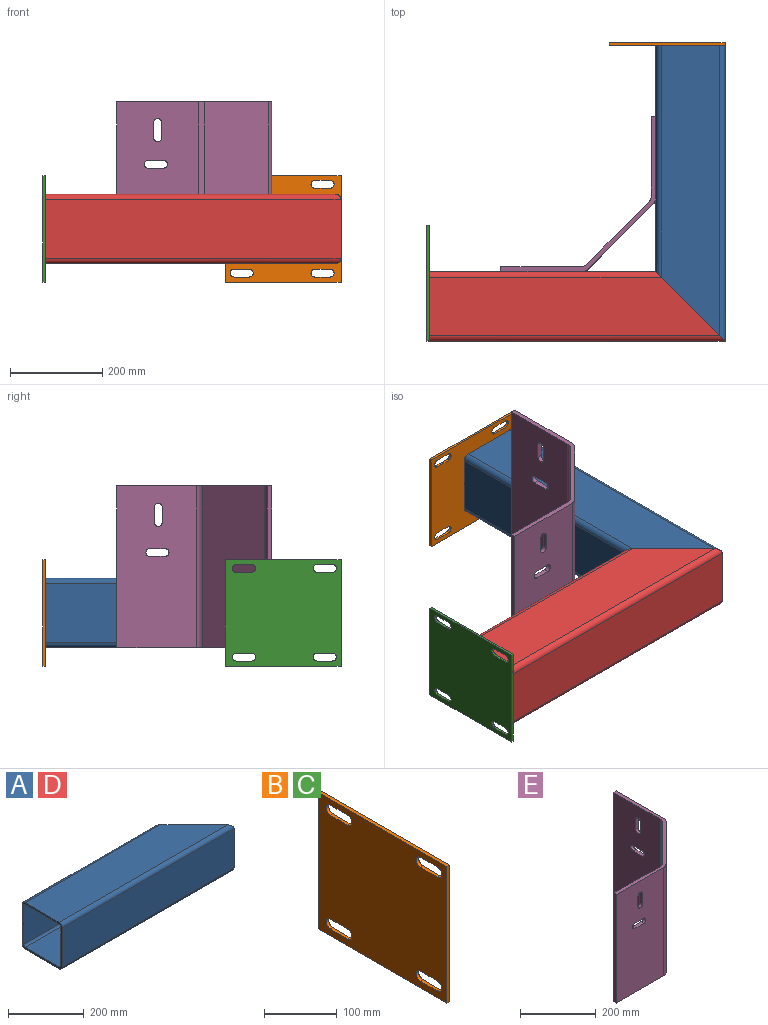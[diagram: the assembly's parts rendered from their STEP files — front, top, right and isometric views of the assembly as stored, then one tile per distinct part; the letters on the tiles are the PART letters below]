
ASSEMBLY  parts=5 mates=7
PART A: 18 faces, bbox 640x150x150 mm
  f0: plane 628x126mm, normal (0,0,-1), area 71190mm2, adj f2,f3,f16,f17
  f1: cylinder r=12mm len=640mm, axis (-1,0,0), area 11981.5mm2, adj f14,f15,f16,f17
  f2: cylinder r=12mm len=640mm, axis (-1,0,0), area 11981.5mm2, adj f0,f14,f16,f17
  f3: cylinder r=12mm len=502mm, axis (-1,0,0), area 9318.5mm2, adj f0,f4,f16,f17
  f4: plane 490x126mm, normal (0,1,0), area 61740mm2, adj f3,f5,f16,f17
  f5: cylinder r=12mm len=502mm, axis (-1,0,0), area 9318.5mm2, adj f4,f15,f16,f17
  f6: plane 633.7x125.4mm, normal (0,1,0), area 79466mm2, adj f7,f13,f16,f17
  f7: cylinder r=6mm len=633.7mm, axis (-1,0,0), area 5951.9mm2, adj f6,f8,f16,f17
  f8: plane 627.7x125.4mm, normal (0,0,-1), area 70851mm2, adj f7,f9,f16,f17
  f9: cylinder r=6mm len=502.3mm, axis (-1,0,0), area 4698.1mm2, adj f8,f10,f16,f17
  f10: plane 496.3x125.4mm, normal (0,-1,0), area 62236mm2, adj f9,f11,f16,f17
  f11: cylinder r=6mm len=502.3mm, axis (-1,0,0), area 4698.1mm2, adj f10,f12,f16,f17
  f12: plane 627.7x125.4mm, normal (0,0,1), area 70851mm2, adj f11,f13,f16,f17
  f13: cylinder r=6mm len=633.7mm, axis (-1,0,0), area 5951.9mm2, adj f6,f12,f16,f17
  f14: plane 640x126mm, normal (0,-1,0), area 80640mm2, adj f1,f2,f16,f17
  f15: plane 628x126mm, normal (0,0,1), area 71190mm2, adj f1,f5,f16,f17
  f16: plane 150x150mm, normal (-1,0,0), area 3528.5mm2, adj f0,f1,f2,f3,f4,f5,f6,f7
  f17: plane 150x150mm, normal (0.71,0.71,0), area 4990.1mm2, adj f0,f1,f2,f3,f4,f5,f6,f7
PART B: 22 faces, bbox 5x250x230 mm
  f0: cylinder r=8.5mm len=17mm, axis (1,0,0), area 133.5mm2, adj f1,f19,f20,f21
  f1: plane 33x5mm, normal (0,0,-1), area 165mm2, adj f0,f2,f20,f21
  f2: cylinder r=8.5mm len=17mm, axis (1,0,0), area 133.5mm2, adj f1,f19,f20,f21
  f3: cylinder r=8.5mm len=17mm, axis (1,0,0), area 133.5mm2, adj f4,f15,f20,f21
  f4: plane 33x5mm, normal (0,0,1), area 165mm2, adj f3,f5,f20,f21
  f5: cylinder r=8.5mm len=17mm, axis (1,0,0), area 133.5mm2, adj f4,f15,f20,f21
  f6: cylinder r=8.5mm len=17mm, axis (1,0,0), area 133.5mm2, adj f7,f16,f20,f21
  f7: plane 33x5mm, normal (0,0,1), area 165mm2, adj f6,f8,f20,f21
  f8: cylinder r=8.5mm len=17mm, axis (1,0,0), area 133.5mm2, adj f7,f16,f20,f21
  f9: cylinder r=8.5mm len=17mm, axis (1,0,0), area 133.5mm2, adj f10,f17,f20,f21
  f10: plane 33x5mm, normal (0,0,1), area 165mm2, adj f9,f11,f20,f21
  f11: cylinder r=8.5mm len=17mm, axis (1,0,0), area 133.5mm2, adj f10,f17,f20,f21
  f12: plane 230x5mm, normal (0,-1,0), area 1150mm2, adj f13,f18,f20,f21
  f13: plane 250x5mm, normal (0,0,1), area 1250mm2, adj f12,f14,f20,f21
  f14: plane 230x5mm, normal (0,1,0), area 1150mm2, adj f13,f18,f20,f21
  f15: plane 33x5mm, normal (0,0,-1), area 165mm2, adj f3,f5,f20,f21
  f16: plane 33x5mm, normal (0,0,-1), area 165mm2, adj f6,f8,f20,f21
  f17: plane 33x5mm, normal (0,0,-1), area 165mm2, adj f9,f11,f20,f21
  f18: plane 250x5mm, normal (0,0,-1), area 1250mm2, adj f12,f14,f20,f21
  f19: plane 33x5mm, normal (0,0,1), area 165mm2, adj f0,f2,f20,f21
  f20: plane 250x230mm, normal (-1,0,0), area 54348.1mm2, adj f0,f1,f2,f3,f4,f5,f6,f7
  f21: plane 250x230mm, normal (1,0,0), area 54348.1mm2, adj f0,f1,f2,f3,f4,f5,f6,f7
PART C: same geometry as B
PART D: same geometry as A
PART E: 30 faces, bbox 335x335x350 mm
  f0: plane 350x10mm, normal (-1,0,0), area 3500mm2, adj f1,f11,f12,f13
  f1: plane 350x175.86mm, normal (0,-1,0), area 59974.3mm2, adj f0,f2,f12,f13,f22,f23,f24,f25
  f2: cylinder r=20mm len=350mm, axis (0,0,-1), area 5497.8mm2, adj f1,f3,f12,f13
  f3: plane 350x139.14mm, normal (0.71,-0.71,0), area 68871.8mm2, adj f2,f4,f12,f13
  f4: cylinder r=20mm len=350mm, axis (0,0,-1), area 5497.8mm2, adj f3,f5,f12,f13
  f5: plane 350x175.86mm, normal (1,0,0), area 59974.3mm2, adj f4,f6,f12,f13,f14,f15,f16,f17
  f6: plane 350x10mm, normal (0,1,0), area 3500mm2, adj f5,f7,f12,f13
  f7: plane 350x171.72mm, normal (-1,0,0), area 58524.5mm2, adj f6,f8,f12,f13,f14,f15,f16,f17
  f8: cylinder r=20mm len=350mm, axis (0,0,-1), area 5497.8mm2, adj f7,f9,f12,f13
  f9: plane 350x133.28mm, normal (-0.71,0.71,0), area 65972.3mm2, adj f8,f10,f12,f13
  f10: cylinder r=20mm len=350mm, axis (0,0,-1), area 5497.8mm2, adj f9,f11,f12,f13
  f11: plane 350x171.72mm, normal (0,1,0), area 58524.5mm2, adj f0,f10,f12,f13,f22,f23,f24,f25
  f12: plane 335x335mm, normal (0,0,1), area 5733.5mm2, adj f0,f1,f2,f3,f4,f5,f6,f7
  f13: plane 335x335mm, normal (0,0,-1), area 5733.5mm2, adj f0,f1,f2,f3,f4,f5,f6,f7
  f14: cylinder r=8.5mm len=17mm, axis (-1,0,0), area 267mm2, adj f5,f7,f15,f17
  f15: plane 33x10mm, normal (0,0,1), area 330mm2, adj f5,f7,f14,f16
  f16: cylinder r=8.5mm len=17mm, axis (-1,0,0), area 267mm2, adj f5,f7,f15,f17
  f17: plane 33x10mm, normal (0,0,-1), area 330mm2, adj f5,f7,f14,f16
  f18: cylinder r=8.5mm len=17mm, axis (-1,0,0), area 267mm2, adj f5,f7,f19,f21
  f19: plane 33x10mm, normal (0,-1,0), area 330mm2, adj f5,f7,f18,f20
  f20: cylinder r=8.5mm len=17mm, axis (-1,0,0), area 267mm2, adj f5,f7,f19,f21
  f21: plane 33x10mm, normal (0,1,0), area 330mm2, adj f5,f7,f18,f20
  f22: cylinder r=8.5mm len=17mm, axis (0,1,0), area 267mm2, adj f1,f11,f23,f25
  f23: plane 33x10mm, normal (0,0,1), area 330mm2, adj f1,f11,f22,f24
  f24: cylinder r=8.5mm len=17mm, axis (0,1,0), area 267mm2, adj f1,f11,f23,f25
  f25: plane 33x10mm, normal (0,0,-1), area 330mm2, adj f1,f11,f22,f24
  f26: cylinder r=8.5mm len=17mm, axis (0,1,0), area 267mm2, adj f1,f11,f27,f29
  f27: plane 33x10mm, normal (-1,0,0), area 330mm2, adj f1,f11,f26,f28
  f28: cylinder r=8.5mm len=17mm, axis (0,1,0), area 267mm2, adj f1,f11,f27,f29
  f29: plane 33x10mm, normal (1,0,0), area 330mm2, adj f1,f11,f26,f28
PLACE A rot(axis=(-0.71,0.71,0),180deg) t=(466.55,478.23,0)mm
PLACE B rot(axis=(0,0,-1),90deg) t=(366.55,478.23,0)mm
PLACE C t=(-98.45,-86.77,0)mm
PLACE D t=(-98.45,-86.77,0)mm
PLACE E t=(224.05,155.73,-75)mm
MATE parallel E.f13 <-> D.f0  axis (0,0,-1) through (283.67,96.11,-75)mm
MATE planar E.f5 <-> A.f4  axis (1,0,0) through (391.55,235.32,98.12)mm
MATE planar B.f21 <-> A.f16  axis (0,-1,0) through (541.55,478.23,0)mm
MATE fastened D.f17 <-> A.f17  axis (0.71,0.71,0) through (541.55,-161.77,0)mm
MATE planar E.f1 <-> D.f4  axis (0,-1,0) through (144.53,-11.77,97.98)mm
MATE planar C.f21 <-> D.f16  axis (1,0,0) through (-98.45,-161.77,0)mm
MATE planar A.f17 <-> D.f17  axis (-0.71,-0.71,0) through (541.55,-161.77,0)mm
